# Revit family: Wire-HunterDouglas-TechStyle_E-Clipped
name_source: partatom
category: Specialty Equipment
revit_build: Autodesk Revit Architecture 2013 (Build: 20120221_2030(x64)
units: mm (PartAtom-declared; Revit-internal decimal feet)

## types (1)
- Wire-HunterDouglas-TechStyle_E-Clipped
    04 CSI = 09 51 00
    95 CSI = 09510
    Acoustics CAC = 17 w/no backer, (ASTM E 1414)
    Acoustics NRC = 0.85 (ASTM C 423)
    Additional Resources Note = Product details, finishes, construction details, and more can be accessed on the Product Page URL.
    Assembly Code = C3030210
    Color Finishes = http://www.hunterdouglascontract.com
    Description = Acoustical Ceiling Panels
    Different Colors Available = No
    EPD URL = In Process
    Fire Rating = Class A (1) (ASTM E 84) (ASTM 1264)
    Flame Spread Index = ≤ 10
    Floating Trim Visibility = No
    GREENGUARD Certified = Yes
    GREENGUARD URL = http://assets.hunterdouglascontract.com
    HPD URL = In Process
    HangerWire Length = 2' - 0"
    Height = 0' - 0"
    High Durability = Yes
    Humidity and Sag Resistant = Yes
    Installation URL = http://assets.hunterdouglascontract.com
    Light Reflectance Average = 0.81
    Manufacturer = Hunter Douglas Luxalon Metal Ceilings
    Material = Metal - Aluminum Frame - HunterDouglas - Painted White
    Model = Techstyle E
    Mold Resistant Note = Resistant to 95% humidity in 104°F temperature
    Panel Length Availability = 6” in increments of 6" up to 72"  and up to 96" (for 24" W Only)
    Panel Width Availability = 24", 30", 48"
    Perforations = http://www.hunterdouglascontract.com
    Product Line = Techstyle Ceilings
    Product Page URL = http://www.hunterdouglascontract.com
    Recyclable = Yes
    Recycled Content Percentage = 7%
    Seismic Info URL = http://assets.hunterdouglascontract.com
    Smoke Developed Index = ≤ 10
    Subcategory = Techstyle E
    Submittal URL = http://assets.hunterdouglascontract.com
    Technical Information = http://assets.hunterdouglascontract.com
    URL = http://www.hunterdouglasceilings.com
    VOC Data URL = http://assets.hunterdouglascontract.com
    Wall Angle Visibility = Yes
    Warranty URL = http://www.hunterdouglascontract.com
    Weight Per Piece Area = 0.0003 ksf
    Width = 0' - 0"
    Wire Hanger = <By Category>
    Wire Visibility = Yes
    ecoScorecard Product Page = http://hunterdouglascontract.ecoscorecard.com
    ecoScorecard_data = http://products.ecoscorecard.com

## geometry (parser evidence)
native form markers: Sweep x1
no freeform markers — native parametric forms only
